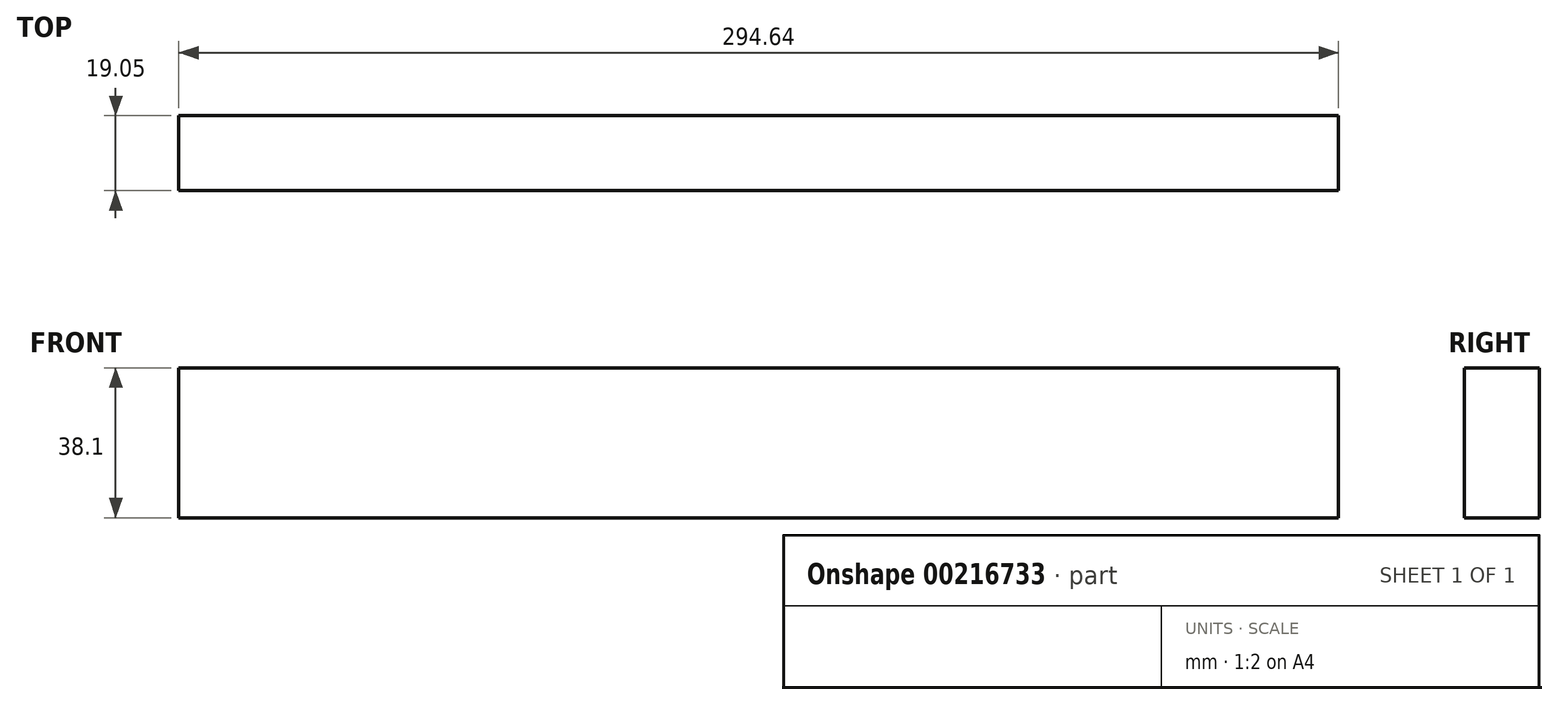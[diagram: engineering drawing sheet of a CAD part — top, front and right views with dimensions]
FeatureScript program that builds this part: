
annotation { "Feature Type Name" : "Feature", "Feature Type Description" : "" }
export const myFeature = defineFeature(function(context is Context, id is Id, definition is map)
    precondition{}
    {
        {
            var Q0;
            Q0=qCreatedBy(makeId("Front.planeOp"),FACE);
            var sketch = newSketch(context, id + "F0", { "sketchPlane" : qUnion([Q0])});
            skLineSegment(sketch, "E0.bottom", {"start": v(0, 0) * mm, "end": v(294.64, 0) * mm});
            skLineSegment(sketch, "E0.top", {"start": v(0, 38.1) * mm, "end": v(294.64, 38.1) * mm});
            skLineSegment(sketch, "E0.left", {"start": v(0, 0) * mm, "end": v(0, 38.1) * mm});
            skLineSegment(sketch, "E0.right", {"start": v(294.64, 0) * mm, "end": v(294.64, 38.1) * mm});
            skSolve(sketch);
        }
        {
            var Q0;
            Q0 = qSketchRegion(id + "F0", true);
            extrude(context, id + "F1", {"entities" : qUnion([Q0]), "depth" : 19.05 * mm});
        }
    });
